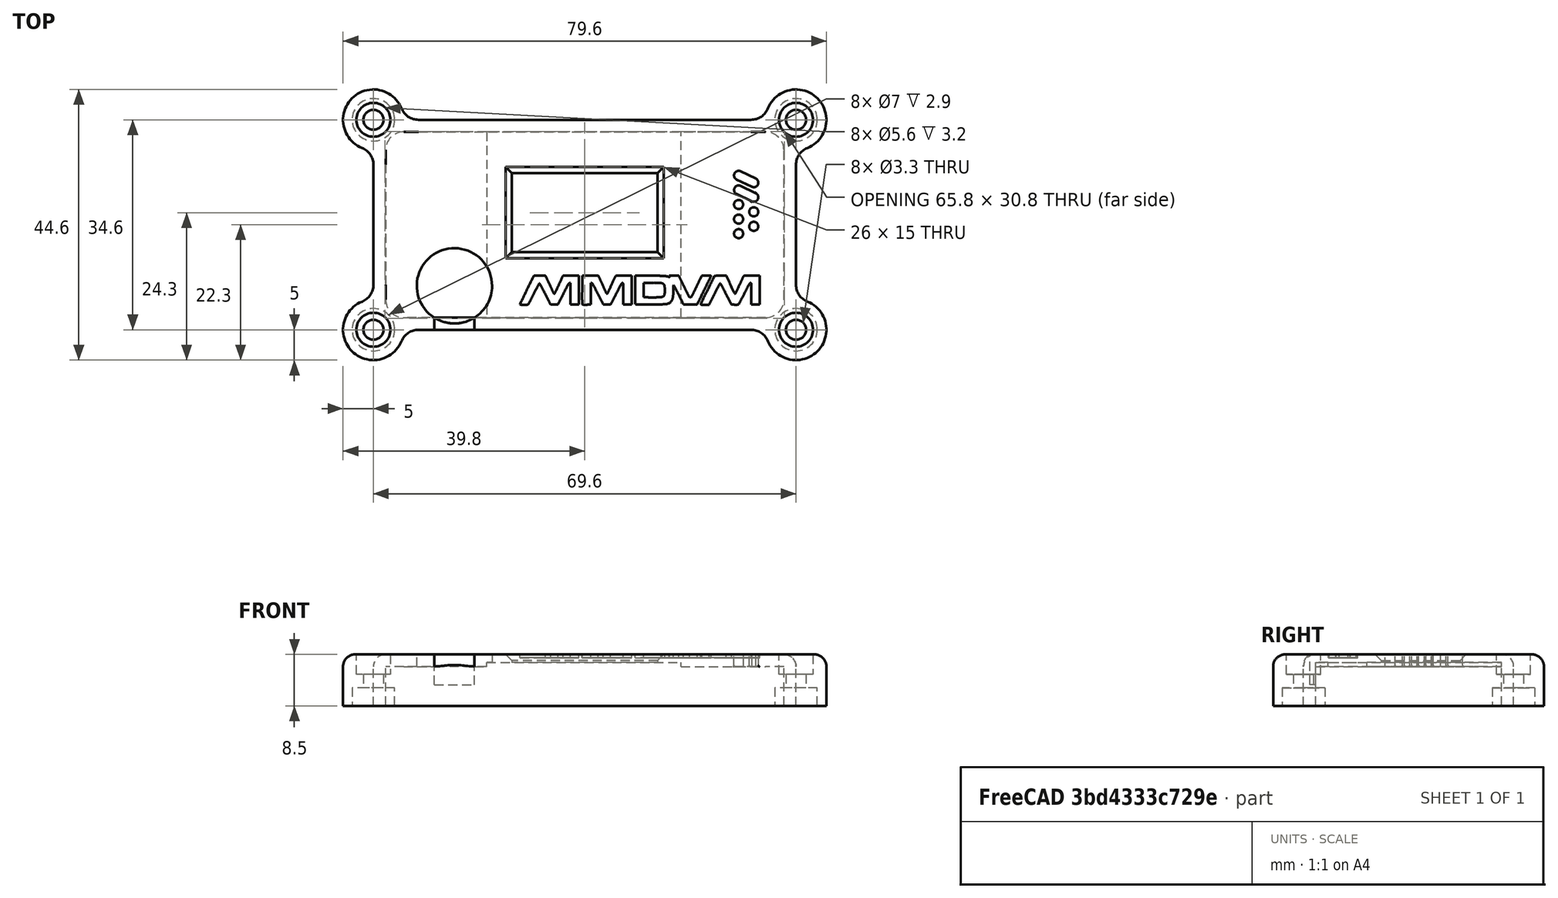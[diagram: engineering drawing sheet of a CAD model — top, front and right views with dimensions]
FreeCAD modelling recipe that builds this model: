
FCSTD DOCUMENT  (FreeCAD 0.18R13964 (Git))
Label: MMDVM_HS_Top-PCB-v1.7-SLIM
License: CreativeCommons Attribution-NonCommercial-ShareAlike
LicenseURL: http://creativecommons.org/licenses/by-nc-sa/4.0/
objects: Sketcher::SketchObject×11, PartDesign::Pocket×6, Part::Feature×5, PartDesign::Fillet×4, Part::Cut×2, Part::FeaturePython×2, PartDesign::Pad×1, PartDesign::Chamfer×1, PartDesign::Hole×1, Part::MultiFuse×1, PartDesign::Body×1, Part::Extrusion×1, Mesh::Feature×1
note: 44 computed .brp shape members not serialized (recipe doc carries the construction recipe); baked Part::Feature solids carry a one-line shape summary decoded from their .brp

FEATURE [Sketcher::SketchObject] Sketch
  MapMode = 5
  Support = -> [XY_Plane]
  sketch-geometry (24):
    g0: LineSegment [constr] StartX=-32.5 StartY=15 StartZ=0 EndX=32.5 EndY=15 EndZ=0
    g1: LineSegment [constr] StartX=32.5 StartY=15 StartZ=0 EndX=32.5 EndY=-15 EndZ=0
    g2: LineSegment [constr] StartX=32.5 StartY=-15 StartZ=0 EndX=-32.5 EndY=-15 EndZ=0
    g3: LineSegment [constr] StartX=-32.5 StartY=-15 StartZ=0 EndX=-32.5 EndY=15 EndZ=0
    g4: LineSegment [constr] StartX=-29 StartY=11.5 StartZ=0 EndX=29 EndY=11.5 EndZ=0
    g5: LineSegment [constr] StartX=29 StartY=11.5 StartZ=0 EndX=29 EndY=-11.5 EndZ=0
    g6: LineSegment [constr] StartX=29 StartY=-11.5 StartZ=0 EndX=-29 EndY=-11.5 EndZ=0
    g7: LineSegment [constr] StartX=-29 StartY=-11.5 StartZ=0 EndX=-29 EndY=11.5 EndZ=0
    g8: Circle CenterX=-29 CenterY=11.5 CenterZ=0 NormalX=0 NormalY=0 NormalZ=1 AngleXU=0 Radius=1.375
    g9: Circle CenterX=29 CenterY=11.5 CenterZ=0 NormalX=0 NormalY=0 NormalZ=1 AngleXU=0 Radius=1.375
    g10: Circle CenterX=29 CenterY=-11.5 CenterZ=0 NormalX=0 NormalY=0 NormalZ=1 AngleXU=0 Radius=1.375
    g11: Circle CenterX=-29 CenterY=-11.5 CenterZ=0 NormalX=0 NormalY=0 NormalZ=1 AngleXU=0 Radius=1.375
    g12: LineSegment [constr] StartX=-29.5 StartY=12 StartZ=0 EndX=29.5 EndY=12 EndZ=0
    g13: LineSegment [constr] StartX=29.5 StartY=12 StartZ=0 EndX=29.5 EndY=-12 EndZ=0
    g14: LineSegment [constr] StartX=29.5 StartY=-12 StartZ=0 EndX=-29.5 EndY=-12 EndZ=0
    g15: LineSegment [constr] StartX=-29.5 StartY=-12 StartZ=0 EndX=-29.5 EndY=12 EndZ=0
    g16: ArcOfCircle CenterX=-29.5 CenterY=12 CenterZ=0 NormalX=0 NormalY=0 NormalZ=1 AngleXU=0 Radius=3 StartAngle=1.5708 EndAngle=3.1416
    g17: ArcOfCircle CenterX=29.5 CenterY=12 CenterZ=0 NormalX=0 NormalY=0 NormalZ=1 AngleXU=0 Radius=3 StartAngle=1.42077e-07 EndAngle=1.5708
    g18: ArcOfCircle CenterX=29.5 CenterY=-12 CenterZ=0 NormalX=0 NormalY=0 NormalZ=1 AngleXU=0 Radius=3 StartAngle=4.71239 EndAngle=6.28319
    g19: ArcOfCircle CenterX=-29.5 CenterY=-12 CenterZ=0 NormalX=0 NormalY=0 NormalZ=1 AngleXU=0 Radius=3 StartAngle=3.14159 EndAngle=4.71239
    g20: LineSegment StartX=-29.5 StartY=15 StartZ=0 EndX=29.5 EndY=15 EndZ=0
    g21: LineSegment StartX=32.5 StartY=12 StartZ=0 EndX=32.5 EndY=-12 EndZ=0
    g22: LineSegment StartX=29.5 StartY=-15 StartZ=0 EndX=-29.5 EndY=-15 EndZ=0
    g23: LineSegment StartX=-32.5 StartY=-12 StartZ=0 EndX=-32.5 EndY=12 EndZ=0
  constraints (68):
    c: Coincident(g0,g1)
    c: Coincident(g1,g2)
    c: Coincident(g2,g3)
    c: Coincident(g3,g0)
    c: Horizontal(g0)
    c: Horizontal(g2)
    c: Vertical(g1)
    c: Vertical(g3)
    c: DistanceX(g0,g0) = 65
    c: DistanceY(g1,g1) = 30
    c: Symmetric(g0,g0,g-2)
    c: Symmetric(g0,g1,g-1)
    c: Coincident(g4,g5)
    c: Coincident(g5,g6)
    c: Coincident(g6,g7)
    c: Coincident(g7,g4)
    c: Horizontal(g4)
    c: Horizontal(g6)
    c: Vertical(g5)
    c: Vertical(g7)
    c: DistanceX(g4,g4) = 58
    c: DistanceY(g5,g5) = 23
    c: Symmetric(g4,g5,g-1)
    c: Symmetric(g4,g4,g-2)
    c: Coincident(g8,g4)
    c: Coincident(g9,g4)
    c: Coincident(g10,g5)
    c: Coincident(g11,g6)
    c: Radius(g11) = 1.375
    c: Radius(g8) = 1.375
    c: Radius(g9) = 1.375
    c: Radius(g10) = 1.375
    c: Coincident(g12,g13)
    c: Coincident(g13,g14)
    c: Coincident(g14,g15)
    c: Coincident(g15,g12)
    c: Horizontal(g12)
    c: Horizontal(g14)
    c: Vertical(g13)
    c: Vertical(g15)
    c: DistanceX(g4,g12) = 0.5
    c: DistanceY(g4,g12) = 0.5
    c: DistanceY(g13,g5) = 0.5
    c: DistanceX(g14,g6) = 0.5
    c: Coincident(g16,g12)
    c: Radius(g16) = 3
    c: Coincident(g17,g12)
    c: Radius(g17) = 3
    c: Coincident(g18,g13)
    c: Radius(g18) = 3
    c: Coincident(g19,g14)
    c: Radius(g19) = 3
    c: PointOnObject(g16,g0)
    c: PointOnObject(g17,g1)
    c: PointOnObject(g18,g2)
    c: PointOnObject(g19,g3)
    c: Coincident(g20,g16)
    c: Horizontal(g20)
    c: Coincident(g20,g17)
    c: Coincident(g21,g17)
    c: Vertical(g21)
    c: Coincident(g18,g21)
    c: Coincident(g22,g18)
    c: Horizontal(g22)
    c: Coincident(g19,g22)
    c: Coincident(g23,g19)
    c: Vertical(g23)
    c: Coincident(g23,g16)
FEATURE [Sketcher::SketchObject] Sketch001
  MapMode = 5
  Support = -> [XY_Plane]
  expr: Constraints[8] = Sketch.Constraints[8]
  expr: Constraints[41] = Sketch.Constraints[41]
  expr: Constraints[9] = Sketch.Constraints[9]
  expr: Constraints[45] = Sketch.Constraints[45]
  expr: Constraints[43] = Sketch.Constraints[43]
  expr: Constraints[42] = Sketch.Constraints[42]
  expr: Constraints[20] = Sketch.Constraints[20]
  expr: Constraints[21] = Sketch.Constraints[21]
  expr: Constraints[28] = Sketch.Constraints[28]
  expr: Constraints[29] = Sketch.Constraints[29]
  expr: Constraints[30] = Sketch.Constraints[30]
  expr: Constraints[40] = Sketch.Constraints[40]
  expr: Constraints[31] = Sketch.Constraints[31]
  expr: Constraints[47] = Sketch.Constraints[47]
  expr: Constraints[49] = Sketch.Constraints[49]
  expr: Constraints[51] = Sketch.Constraints[51]
  sketch-geometry (64):
    g0: LineSegment [constr] StartX=-32.5 StartY=15 StartZ=0 EndX=32.5 EndY=15 EndZ=0
    g1: LineSegment [constr] StartX=32.5 StartY=15 StartZ=0 EndX=32.5 EndY=-15 EndZ=0
    g2: LineSegment [constr] StartX=32.5 StartY=-15 StartZ=0 EndX=-32.5 EndY=-15 EndZ=0
    g3: LineSegment [constr] StartX=-32.5 StartY=-15 StartZ=0 EndX=-32.5 EndY=15 EndZ=0
    g4: LineSegment [constr] StartX=-29 StartY=11.5 StartZ=0 EndX=29 EndY=11.5 EndZ=0
    g5: LineSegment [constr] StartX=29 StartY=11.5 StartZ=0 EndX=29 EndY=-11.5 EndZ=0
    g6: LineSegment [constr] StartX=29 StartY=-11.5 StartZ=0 EndX=-29 EndY=-11.5 EndZ=0
    g7: LineSegment [constr] StartX=-29 StartY=-11.5 StartZ=0 EndX=-29 EndY=11.5 EndZ=0
    g8: Circle [constr] CenterX=-29 CenterY=11.5 CenterZ=0 NormalX=0 NormalY=0 NormalZ=1 AngleXU=0 Radius=1.375
    g9: Circle [constr] CenterX=29 CenterY=11.5 CenterZ=0 NormalX=0 NormalY=0 NormalZ=1 AngleXU=0 Radius=1.375
    g10: Circle [constr] CenterX=29 CenterY=-11.5 CenterZ=0 NormalX=0 NormalY=0 NormalZ=1 AngleXU=0 Radius=1.375
    g11: Circle [constr] CenterX=-29 CenterY=-11.5 CenterZ=0 NormalX=0 NormalY=0 NormalZ=1 AngleXU=0 Radius=1.375
    g12: LineSegment [constr] StartX=-29.5 StartY=12 StartZ=0 EndX=29.5 EndY=12 EndZ=0
    g13: LineSegment [constr] StartX=29.5 StartY=12 StartZ=0 EndX=29.5 EndY=-12 EndZ=0
    g14: LineSegment [constr] StartX=29.5 StartY=-12 StartZ=0 EndX=-29.5 EndY=-12 EndZ=0
    g15: LineSegment [constr] StartX=-29.5 StartY=-12 StartZ=0 EndX=-29.5 EndY=12 EndZ=0
    g16: ArcOfCircle [constr] CenterX=-29.5 CenterY=12 CenterZ=0 NormalX=0 NormalY=0 NormalZ=1 AngleXU=0 Radius=3 StartAngle=1.5708 EndAngle=3.14159
    g17: ArcOfCircle [constr] CenterX=29.5 CenterY=12 CenterZ=0 NormalX=0 NormalY=0 NormalZ=1 AngleXU=0 Radius=3 StartAngle=2.8425e-08 EndAngle=1.5708
    g18: ArcOfCircle [constr] CenterX=29.5 CenterY=-12 CenterZ=0 NormalX=0 NormalY=0 NormalZ=1 AngleXU=0 Radius=3 StartAngle=4.71239 EndAngle=6.28319
    g19: ArcOfCircle [constr] CenterX=-29.5 CenterY=-12 CenterZ=0 NormalX=0 NormalY=0 NormalZ=1 AngleXU=0 Radius=3 StartAngle=3.14159 EndAngle=4.71239
    g20: LineSegment [constr] StartX=-29.5 StartY=15 StartZ=0 EndX=29.5 EndY=15 EndZ=0
    g21: LineSegment [constr] StartX=32.5 StartY=12 StartZ=0 EndX=32.5 EndY=-12 EndZ=0
    g22: LineSegment [constr] StartX=29.5 StartY=-15 StartZ=0 EndX=-29.5 EndY=-15 EndZ=0
    g23: LineSegment [constr] StartX=-32.5 StartY=-12 StartZ=0 EndX=-32.5 EndY=12 EndZ=0
    g24: ArcOfCircle [constr] CenterX=-29.5 CenterY=12 CenterZ=0 NormalX=0 NormalY=0 NormalZ=1 AngleXU=0 Radius=3.3 StartAngle=1.5708 EndAngle=3.14159
    g25: ArcOfCircle [constr] CenterX=29.5 CenterY=12 CenterZ=0 NormalX=0 NormalY=0 NormalZ=1 AngleXU=0 Radius=3.3 StartAngle=-2.2e-10 EndAngle=1.5708
    g26: ArcOfCircle [constr] CenterX=29.5 CenterY=-12 CenterZ=0 NormalX=0 NormalY=0 NormalZ=1 AngleXU=0 Radius=3.3 StartAngle=4.71239 EndAngle=6.28319
    g27: ArcOfCircle [constr] CenterX=-29.5 CenterY=-12 CenterZ=0 NormalX=0 NormalY=0 NormalZ=1 AngleXU=0 Radius=3.3 StartAngle=3.14159 EndAngle=4.71239
    g28: LineSegment [constr] StartX=-32.8 StartY=12 StartZ=0 EndX=-32.8 EndY=-12 EndZ=0
    g29: LineSegment [constr] StartX=-29.5 StartY=15.3 StartZ=0 EndX=29.5 EndY=15.3 EndZ=0
    g30: LineSegment [constr] StartX=32.8 StartY=12 StartZ=0 EndX=32.8 EndY=-12 EndZ=0
    g31: LineSegment [constr] StartX=29.5 StartY=-15.3 StartZ=0 EndX=-29.5 EndY=-15.3 EndZ=0
    g32: LineSegment [constr] StartX=-34.8 StartY=17.3 StartZ=0 EndX=34.8 EndY=17.3 EndZ=0
    g33: LineSegment [constr] StartX=34.8 StartY=17.3 StartZ=0 EndX=34.8 EndY=-17.3 EndZ=0
    g34: LineSegment [constr] StartX=34.8 StartY=-17.3 StartZ=0 EndX=-34.8 EndY=-17.3 EndZ=0
    g35: LineSegment [constr] StartX=-34.8 StartY=-17.3 StartZ=0 EndX=-34.8 EndY=17.3 EndZ=0
    g36: Circle [constr] CenterX=34.8 CenterY=17.3 CenterZ=0 NormalX=0 NormalY=0 NormalZ=1 AngleXU=0 Radius=5
    g37: Circle [constr] CenterX=34.8 CenterY=-17.3 CenterZ=0 NormalX=0 NormalY=0 NormalZ=1 AngleXU=0 Radius=5
    g38: Circle [constr] CenterX=-34.8 CenterY=-17.3 CenterZ=0 NormalX=0 NormalY=0 NormalZ=1 AngleXU=0 Radius=5
    g39: Circle [constr] CenterX=-34.8 CenterY=17.3 CenterZ=0 NormalX=0 NormalY=0 NormalZ=1 AngleXU=0 Radius=5
    g40: Circle [constr] CenterX=27.3838 CenterY=20.3 CenterZ=0 NormalX=0 NormalY=0 NormalZ=1 AngleXU=0 Radius=3
    g41: Circle [constr] CenterX=-27.3838 CenterY=20.3 CenterZ=0 NormalX=0 NormalY=0 NormalZ=1 AngleXU=0 Radius=3
    g42: Circle [constr] CenterX=-37.8 CenterY=9.8838 CenterZ=0 NormalX=0 NormalY=0 NormalZ=1 AngleXU=0 Radius=3
    g43: Circle [constr] CenterX=-37.8 CenterY=-9.8838 CenterZ=0 NormalX=0 NormalY=0 NormalZ=1 AngleXU=0 Radius=3
    g44: Circle [constr] CenterX=-27.3838 CenterY=-20.3 CenterZ=0 NormalX=0 NormalY=0 NormalZ=1 AngleXU=0 Radius=3
    g45: Circle [constr] CenterX=27.3838 CenterY=-20.3 CenterZ=0 NormalX=0 NormalY=0 NormalZ=1 AngleXU=0 Radius=3
    g46: Circle [constr] CenterX=37.8 CenterY=-9.8838 CenterZ=0 NormalX=0 NormalY=0 NormalZ=1 AngleXU=0 Radius=3
    g47: Circle [constr] CenterX=37.8 CenterY=9.8838 CenterZ=0 NormalX=0 NormalY=0 NormalZ=1 AngleXU=0 Radius=3
    g48: ArcOfCircle CenterX=34.8 CenterY=17.3 CenterZ=0 NormalX=0 NormalY=0 NormalZ=1 AngleXU=0 Radius=5 StartAngle=5.09679 EndAngle=9.04038
    g49: ArcOfCircle CenterX=27.3838 CenterY=20.3 CenterZ=0 NormalX=0 NormalY=0 NormalZ=1 AngleXU=0 Radius=3 StartAngle=4.71239 EndAngle=5.89879
    g50: ArcOfCircle CenterX=37.8 CenterY=9.8838 CenterZ=0 NormalX=0 NormalY=0 NormalZ=1 AngleXU=0 Radius=3 StartAngle=1.95519 EndAngle=3.14159
    g51: ArcOfCircle CenterX=37.8 CenterY=-9.8838 CenterZ=0 NormalX=0 NormalY=0 NormalZ=1 AngleXU=0 Radius=3 StartAngle=3.14159 EndAngle=4.32799
    g52: ArcOfCircle CenterX=34.8 CenterY=-17.3 CenterZ=0 NormalX=0 NormalY=0 NormalZ=1 AngleXU=0 Radius=5 StartAngle=3.52599 EndAngle=7.46958
    g53: ArcOfCircle CenterX=27.3838 CenterY=-20.3 CenterZ=0 NormalX=0 NormalY=0 NormalZ=1 AngleXU=0 Radius=3 StartAngle=0.384397 EndAngle=1.5708
    g54: ArcOfCircle CenterX=-27.3838 CenterY=-20.3 CenterZ=0 NormalX=0 NormalY=0 NormalZ=1 AngleXU=0 Radius=3 StartAngle=1.5708 EndAngle=2.7572
    g55: ArcOfCircle CenterX=-34.8 CenterY=-17.3 CenterZ=0 NormalX=0 NormalY=0 NormalZ=1 AngleXU=0 Radius=5 StartAngle=1.95519 EndAngle=5.89879
    g56: ArcOfCircle CenterX=-37.8 CenterY=-9.8838 CenterZ=0 NormalX=0 NormalY=0 NormalZ=1 AngleXU=0 Radius=3 StartAngle=5.09679 EndAngle=6.28319
    g57: ArcOfCircle CenterX=-37.8 CenterY=9.8838 CenterZ=0 NormalX=0 NormalY=0 NormalZ=1 AngleXU=0 Radius=3 StartAngle=6.28319 EndAngle=7.46958
    g58: ArcOfCircle CenterX=-34.8 CenterY=17.3 CenterZ=0 NormalX=0 NormalY=0 NormalZ=1 AngleXU=0 Radius=5 StartAngle=0.384397 EndAngle=4.32799
    g59: ArcOfCircle CenterX=-27.3838 CenterY=20.3 CenterZ=0 NormalX=0 NormalY=0 NormalZ=1 AngleXU=0 Radius=3 StartAngle=3.52599 EndAngle=4.71239
    g60: LineSegment StartX=-27.3838 StartY=17.3 StartZ=0 EndX=27.3838 EndY=17.3 EndZ=0
    g61: LineSegment StartX=34.8 StartY=9.8838 StartZ=0 EndX=34.8 EndY=-9.8838 EndZ=0
    g62: LineSegment StartX=27.3838 StartY=-17.3 StartZ=0 EndX=-27.3838 EndY=-17.3 EndZ=0
    g63: LineSegment StartX=-34.8 StartY=-9.8838 StartZ=0 EndX=-34.8 EndY=9.8838 EndZ=0
  constraints (184):
    c: Coincident(g0,g1)
    c: Coincident(g1,g2)
    c: Coincident(g2,g3)
    c: Coincident(g3,g0)
    c: Horizontal(g0)
    c: Horizontal(g2)
    c: Vertical(g1)
    c: Vertical(g3)
    c: DistanceX(g0,g0) = 65
    c: DistanceY(g1,g1) = 30
    c: Symmetric(g0,g0,g-2)
    c: Symmetric(g0,g1,g-1)
    c: Coincident(g4,g5)
    c: Coincident(g5,g6)
    c: Coincident(g6,g7)
    c: Coincident(g7,g4)
    c: Horizontal(g4)
    c: Horizontal(g6)
    c: Vertical(g5)
    c: Vertical(g7)
    c: DistanceX(g4,g4) = 58
    c: DistanceY(g5,g5) = 23
    c: Symmetric(g4,g5,g-1)
    c: Symmetric(g4,g4,g-2)
    c: Coincident(g8,g4)
    c: Coincident(g9,g4)
    c: Coincident(g10,g5)
    c: Coincident(g11,g6)
    c: Radius(g11) = 1.375
    c: Radius(g8) = 1.375
    c: Radius(g9) = 1.375
    c: Radius(g10) = 1.375
    c: Coincident(g12,g13)
    c: Coincident(g13,g14)
    c: Coincident(g14,g15)
    c: Coincident(g15,g12)
    c: Horizontal(g12)
    c: Horizontal(g14)
    c: Vertical(g13)
    c: Vertical(g15)
    c: DistanceX(g4,g12) = 0.5
    c: DistanceY(g4,g12) = 0.5
    c: DistanceY(g13,g5) = 0.5
    c: DistanceX(g14,g6) = 0.5
    c: Coincident(g16,g12)
    c: Radius(g16) = 3
    c: Coincident(g17,g12)
    c: Radius(g17) = 3
    c: Coincident(g18,g13)
    c: Radius(g18) = 3
    c: Coincident(g19,g14)
    c: Radius(g19) = 3
    c: PointOnObject(g16,g0)
    c: PointOnObject(g17,g1)
    c: PointOnObject(g18,g2)
    c: PointOnObject(g19,g3)
    c: Coincident(g20,g16)
    c: Horizontal(g20)
    c: Coincident(g20,g17)
    c: Coincident(g21,g17)
    c: Vertical(g21)
    c: Coincident(g18,g21)
    c: Coincident(g22,g18)
    c: Horizontal(g22)
    c: Coincident(g19,g22)
    c: Coincident(g23,g19)
    c: Vertical(g23)
    c: Coincident(g23,g16)
    c: Coincident(g24,g12)
    c: Radius(g24) = 3.3
    c: Coincident(g25,g12)
    c: Radius(g25) = 3.3
    c: Coincident(g26,g13)
    c: Radius(g26) = 3.3
    c: Coincident(g27,g14)
    c: Radius(g27) = 3.3
    c: Vertical(g28)
    c: DistanceX(g28,g2) = 0.3
    c: Coincident(g27,g28)
    c: Coincident(g28,g24)
    c: Horizontal(g29)
    c: DistanceY(g0,g29) = 0.3
    c: Coincident(g24,g29)
    c: Coincident(g25,g29)
    c: Vertical(g30)
    c: DistanceX(g0,g30) = 0.3
    c: Coincident(g25,g30)
    c: Coincident(g30,g26)
    c: Horizontal(g31)
    c: DistanceY(g31,g1) = 0.3
    c: Coincident(g31,g26)
    c: Coincident(g31,g27)
    c: Coincident(g32,g33)
    c: Coincident(g33,g34)
    c: Coincident(g34,g35)
    c: Coincident(g35,g32)
    c: Horizontal(g32)
    c: Horizontal(g34)
    c: Vertical(g33)
    c: Vertical(g35)
    c: DistanceY(g25,g32) = 2
    c: DistanceX(g25,g32) = 2
    c: DistanceY(g33,g26) = 2
    c: DistanceX(g34,g27) = 2
    c: Coincident(g36,g32)
    c: Coincident(g37,g33)
    c: Coincident(g38,g34)
    c: Coincident(g39,g32)
    c: Radius(g39) = 5
    c: Radius(g38) = 5
    c: Radius(g37) = 5
    c: Radius(g36) = 5
    c: Radius(g40) = 3
    c: Tangent(g40,g36)
    c: Tangent(g40,g32)
    c: Tangent(g47,g36)
    c: Radius(g47) = 3
    c: Tangent(g47,g33)
    c: Radius(g46) = 3
    c: Tangent(g46,g37)
    c: Tangent(g46,g33)
    c: Radius(g45) = 3
    c: Tangent(g45,g37)
    c: Tangent(g45,g34)
    c: Radius(g44) = 3
    c: Tangent(g44,g34)
    c: Tangent(g44,g38)
    c: Radius(g43) = 3
    c: Tangent(g43,g38)
    c: Tangent(g43,g35)
    c: Radius(g42) = 3
    c: Tangent(g42,g35)
    c: Tangent(g42,g39)
    c: Radius(g41) = 3
    c: Tangent(g41,g32)
    c: Tangent(g41,g39)
    c: Coincident(g48,g32)
    c: PointOnObject(g48,g36)
    c: Coincident(g49,g40)
    c: PointOnObject(g49,g40)
    c: Coincident(g50,g47)
    c: PointOnObject(g50,g47)
    c: Coincident(g51,g46)
    c: PointOnObject(g51,g46)
    c: Coincident(g52,g33)
    c: PointOnObject(g52,g37)
    c: Coincident(g53,g45)
    c: PointOnObject(g53,g45)
    c: Coincident(g54,g44)
    c: PointOnObject(g54,g44)
    c: Coincident(g55,g34)
    c: PointOnObject(g55,g38)
    c: Coincident(g56,g43)
    c: PointOnObject(g56,g43)
    c: Coincident(g57,g42)
    c: PointOnObject(g57,g42)
    c: Coincident(g58,g32)
    c: PointOnObject(g58,g39)
    c: Coincident(g59,g41)
    c: PointOnObject(g59,g41)
    c: Coincident(g49,g48)
    c: Coincident(g48,g50)
    c: Coincident(g51,g52)
    c: Coincident(g52,g53)
    c: Coincident(g54,g55)
    c: Coincident(g55,g56)
    c: Coincident(g57,g58)
    c: Coincident(g58,g59)
    c: PointOnObject(g60,g32)
    c: Horizontal(g60)
    c: PointOnObject(g61,g33)
    c: Vertical(g61)
    c: PointOnObject(g62,g34)
    c: Horizontal(g62)
    c: PointOnObject(g63,g35)
    c: Vertical(g63)
    c: Coincident(g59,g60)
    c: Coincident(g60,g49)
    c: Coincident(g50,g61)
    c: Coincident(g61,g51)
    c: Coincident(g53,g62)
    c: Coincident(g54,g62)
    c: Coincident(g56,g63)
    c: Coincident(g57,g63)
FEATURE [PartDesign::Pad] Pad
  Length = 8.5
  Length2 = 100
  Profile = -> Sketch001
  Type = 0
FEATURE [Sketcher::SketchObject] Sketch002
  ExternalGeometry = -> [Pad]
  MapMode = 5
  Placement = pos=(0,0,0) rot=(1,0,0;3.14159rad)
  Support = -> [Pad]
  sketch-geometry (4):
    g0: Circle CenterX=34.8 CenterY=17.3 CenterZ=0 NormalX=0 NormalY=0 NormalZ=1 AngleXU=0 Radius=3.5
    g1: Circle CenterX=34.8 CenterY=-17.3 CenterZ=0 NormalX=0 NormalY=0 NormalZ=1 AngleXU=0 Radius=3.5
    g2: Circle CenterX=-34.8 CenterY=-17.3 CenterZ=0 NormalX=0 NormalY=0 NormalZ=1 AngleXU=0 Radius=3.5
    g3: Circle CenterX=-34.8 CenterY=17.3 CenterZ=0 NormalX=0 NormalY=0 NormalZ=1 AngleXU=0 Radius=3.5
  constraints (8):
    c: Coincident(g0,g-3)
    c: Radius(g0) = 3.5
    c: Coincident(g1,g-6)
    c: Radius(g1) = 3.5
    c: Coincident(g2,g-5)
    c: Radius(g2) = 3.5
    c: Coincident(g3,g-4)
    c: Radius(g3) = 3.5
FEATURE [PartDesign::Pocket] Pocket
  BaseFeature = -> Pad
  Length = 3
  Length2 = 1
  Profile = -> Sketch002
  Type = 0
FEATURE [Sketcher::SketchObject] Sketch003
  MapMode = 5
  Placement = pos=(0,0,0) rot=(1,0,0;3.14159rad)
  Support = -> [Pocket]
  expr: Constraints[8] = Sketch.Constraints[8]
  expr: Constraints[39] = Sketch.Constraints[40]
  expr: Constraints[30] = Sketch.Constraints[31]
  expr: Constraints[27] = Sketch.Constraints[28]
  expr: Constraints[29] = Sketch.Constraints[30]
  expr: Constraints[28] = Sketch.Constraints[29]
  expr: Constraints[20] = -Sketch.Constraints[21]
  expr: Constraints[19] = Sketch.Constraints[20]
  expr: Constraints[42] = Sketch.Constraints[43]
  expr: Constraints[41] = -Sketch.Constraints[42]
  expr: Constraints[9] = -Sketch.Constraints[9]
  expr: Constraints[40] = -Sketch.Constraints[41]
  sketch-geometry (32):
    g0: LineSegment [constr] StartX=-32.5 StartY=-15 StartZ=0 EndX=32.5 EndY=-15 EndZ=0
    g1: LineSegment [constr] StartX=32.5 StartY=-15 StartZ=0 EndX=32.5 EndY=15 EndZ=0
    g2: LineSegment [constr] StartX=32.5 StartY=15 StartZ=0 EndX=-32.5 EndY=15 EndZ=0
    g3: LineSegment [constr] StartX=-32.5 StartY=15 StartZ=0 EndX=-32.5 EndY=-15 EndZ=0
    g4: LineSegment [constr] StartX=-29 StartY=-11.5 StartZ=0 EndX=29 EndY=-11.5 EndZ=0
    g5: LineSegment [constr] StartX=29 StartY=-11.5 StartZ=0 EndX=29 EndY=11.5 EndZ=0
    g6: LineSegment [constr] StartX=29 StartY=11.5 StartZ=0 EndX=-29 EndY=11.5 EndZ=0
    g7: LineSegment [constr] StartX=-29 StartY=11.5 StartZ=0 EndX=-29 EndY=-11.5 EndZ=0
    g8: Circle [constr] CenterX=-29 CenterY=-11.5 CenterZ=0 NormalX=0 NormalY=0 NormalZ=1 AngleXU=0 Radius=1.375
    g9: Circle [constr] CenterX=29 CenterY=-11.5 CenterZ=0 NormalX=0 NormalY=0 NormalZ=1 AngleXU=0 Radius=1.375
    g10: Circle [constr] CenterX=29 CenterY=11.5 CenterZ=0 NormalX=0 NormalY=0 NormalZ=1 AngleXU=0 Radius=1.375
    g11: Circle [constr] CenterX=-29 CenterY=11.5 CenterZ=0 NormalX=0 NormalY=0 NormalZ=1 AngleXU=0 Radius=1.375
    g12: LineSegment [constr] StartX=-29.5 StartY=-12 StartZ=0 EndX=29.5 EndY=-12 EndZ=0
    g13: LineSegment [constr] StartX=29.5 StartY=-12 StartZ=0 EndX=29.5 EndY=12 EndZ=0
    g14: LineSegment [constr] StartX=29.5 StartY=12 StartZ=0 EndX=-29.5 EndY=12 EndZ=0
    g15: LineSegment [constr] StartX=-29.5 StartY=12 StartZ=0 EndX=-29.5 EndY=-12 EndZ=0
    g16: LineSegment [constr] StartX=-29.5121 StartY=-15 StartZ=0 EndX=29.5 EndY=-15 EndZ=0
    g17: LineSegment [constr] StartX=32.5 StartY=-12 StartZ=0 EndX=32.5 EndY=12 EndZ=0
    g18: LineSegment [constr] StartX=29.5 StartY=15 StartZ=0 EndX=-29.5121 EndY=15 EndZ=0
    g19: LineSegment [constr] StartX=-32.5 StartY=12 StartZ=0 EndX=-32.5 EndY=-12 EndZ=0
    g20: ArcOfCircle [constr] CenterX=-29.5 CenterY=12 CenterZ=0 NormalX=0 NormalY=0 NormalZ=1 AngleXU=0 Radius=3.00002 StartAngle=1.57483 EndAngle=3.1416
    g21: ArcOfCircle [constr] CenterX=29.5 CenterY=12 CenterZ=0 NormalX=0 NormalY=0 NormalZ=1 AngleXU=0 Radius=3 StartAngle=6.28318 EndAngle=7.85399
    g22: ArcOfCircle [constr] CenterX=29.5 CenterY=-12 CenterZ=0 NormalX=0 NormalY=0 NormalZ=1 AngleXU=0 Radius=3 StartAngle=4.71238 EndAngle=6.28319
    g23: ArcOfCircle [constr] CenterX=-29.5 CenterY=-12 CenterZ=0 NormalX=0 NormalY=0 NormalZ=1 AngleXU=0 Radius=3.00002 StartAngle=3.14159 EndAngle=4.70836
    g24: LineSegment StartX=-29.8 StartY=15.3 StartZ=0 EndX=29.8 EndY=15.3 EndZ=0
    g25: LineSegment StartX=32.8 StartY=12.3 StartZ=0 EndX=32.8 EndY=-12.3 EndZ=0
    g26: LineSegment StartX=29.8 StartY=-15.3 StartZ=0 EndX=-29.8 EndY=-15.3 EndZ=0
    g27: LineSegment StartX=-32.8 StartY=-12.3 StartZ=0 EndX=-32.8 EndY=12.3 EndZ=0
    g28: ArcOfCircle CenterX=29.8 CenterY=12.3 CenterZ=0 NormalX=0 NormalY=0 NormalZ=1 AngleXU=0 Radius=3 StartAngle=0 EndAngle=1.5708
    g29: ArcOfCircle CenterX=29.8 CenterY=-12.3 CenterZ=0 NormalX=0 NormalY=0 NormalZ=1 AngleXU=0 Radius=3 StartAngle=4.71239 EndAngle=6.28319
    g30: ArcOfCircle CenterX=-29.8 CenterY=-12.3 CenterZ=0 NormalX=0 NormalY=0 NormalZ=1 AngleXU=0 Radius=3 StartAngle=3.14159 EndAngle=4.71239
    g31: ArcOfCircle CenterX=-29.8 CenterY=12.3 CenterZ=0 NormalX=0 NormalY=0 NormalZ=1 AngleXU=0 Radius=3 StartAngle=1.5708 EndAngle=3.14159
  constraints (83):
    c: Coincident(g0,g1)
    c: Coincident(g1,g2)
    c: Coincident(g2,g3)
    c: Coincident(g3,g0)
    c: Horizontal(g0)
    c: Horizontal(g2)
    c: Vertical(g1)
    c: Vertical(g3)
    c: DistanceX(g0,g0) = 65
    c: DistanceY(g1,g1) = -30
    c: Symmetric(g0,g0,g-2)
    c: Symmetric(g0,g1,g-1)
    c: Coincident(g4,g5)
    c: Coincident(g5,g6)
    c: Coincident(g6,g7)
    c: Horizontal(g4)
    c: Horizontal(g6)
    c: Vertical(g5)
    c: Vertical(g7)
    c: DistanceX(g4,g4) = 58
    c: DistanceY(g5,g5) = -23
    c: Symmetric(g4,g5,g-1)
    c: Symmetric(g4,g4,g-2)
    c: Coincident(g8,g4)
    c: Coincident(g9,g4)
    c: Coincident(g10,g5)
    c: Coincident(g11,g6)
    c: Radius(g11) = 1.375
    c: Radius(g8) = 1.375
    c: Radius(g9) = 1.375
    c: Radius(g10) = 1.375
    c: Coincident(g12,g13)
    c: Coincident(g13,g14)
    c: Coincident(g14,g15)
    c: Coincident(g15,g12)
    c: Horizontal(g12)
    c: Horizontal(g14)
    c: Vertical(g13)
    c: Vertical(g15)
    c: DistanceX(g4,g12) = 0.5
    c: DistanceY(g4,g12) = -0.5
    c: DistanceY(g13,g5) = -0.5
    c: DistanceX(g14,g6) = 0.5
    c: PointOnObject(g16,g0)
    c: PointOnObject(g17,g1)
    c: PointOnObject(g18,g2)
    c: PointOnObject(g19,g3)
    c: Horizontal(g16)
    c: Vertical(g17)
    c: Horizontal(g18)
    c: Vertical(g19)
    c: Coincident(g20,g14)
    c: Coincident(g20,g18)
    c: Coincident(g20,g19)
    c: Coincident(g21,g13)
    c: Coincident(g21,g17)
    c: Coincident(g21,g18)
    c: Coincident(g22,g12)
    c: Coincident(g22,g16)
    c: Coincident(g22,g17)
    c: Coincident(g23,g12)
    c: Coincident(g23,g19)
    c: Coincident(g23,g16)
    c: Horizontal(g24)
    c: Horizontal(g26)
    c: Vertical(g25)
    c: Vertical(g27)
    c: Tangent(g24,g28) = 1.5708
    c: Tangent(g25,g28) = 1.5708
    c: Tangent(g25,g29) = 1.5708
    c: Tangent(g26,g29) = 1.5708
    c: Tangent(g26,g30) = 1.5708
    c: Tangent(g27,g30) = 1.5708
    c: Tangent(g27,g31) = 1.5708
    c: Tangent(g24,g31) = 1.5708
    c: Radius(g31) = 3
    c: Radius(g28) = 3
    c: Radius(g29) = 3
    c: Radius(g30) = 3
    c: DistanceY(g1,g24) = 0.3
    c: DistanceX(g17,g25) = 0.3
    c: DistanceY(g26,g16) = 0.3
    c: DistanceX(g27,g19) = 0.3
FEATURE [PartDesign::Pocket] Pocket001
  BaseFeature = -> Pocket
  Length = 6.5
  Length2 = 100
  Profile = -> Sketch003
  Type = 0
FEATURE [Sketcher::SketchObject] Sketch004
  ExternalGeometry = -> [Pocket001]
  MapMode = 5
  Placement = pos=(0,0,8.5) rot=(0,0,1;0rad)
  Support = -> [Pocket001]
  sketch-geometry (32):
    g0: LineSegment StartX=-27.3838 StartY=17.3 StartZ=0 EndX=-31.8 EndY=17.3 EndZ=0
    g1: LineSegment StartX=-34.8 StartY=9.8838 StartZ=0 EndX=-34.8 EndY=14.3 EndZ=0
    g2: Circle [constr] CenterX=-31.8 CenterY=14.3 CenterZ=0 NormalX=0 NormalY=0 NormalZ=1 AngleXU=0 Radius=3
    g3: ArcOfCircle CenterX=-31.8 CenterY=14.3 CenterZ=0 NormalX=0 NormalY=0 NormalZ=1 AngleXU=0 Radius=3 StartAngle=1.5708 EndAngle=3.14159
    g4: LineSegment StartX=-41.7809 StartY=24.2149 StartZ=0 EndX=-27.3838 EndY=24.2149 EndZ=0
    g5: LineSegment StartX=-41.7809 StartY=9.8838 StartZ=0 EndX=-41.7809 EndY=24.2149 EndZ=0
    g6: LineSegment StartX=-27.3838 StartY=24.2149 StartZ=0 EndX=-27.3838 EndY=17.3 EndZ=0
    g7: LineSegment StartX=-41.7809 StartY=9.8838 StartZ=0 EndX=-34.8 EndY=9.8838 EndZ=0
    g8: LineSegment StartX=27.3838 StartY=17.3 StartZ=0 EndX=31.8 EndY=17.3 EndZ=0
    g9: LineSegment StartX=34.8 StartY=9.8838 StartZ=0 EndX=34.8 EndY=14.3 EndZ=0
    g10: Circle [constr] CenterX=31.8 CenterY=14.3 CenterZ=0 NormalX=0 NormalY=0 NormalZ=1 AngleXU=0 Radius=3
    g11: ArcOfCircle CenterX=31.8 CenterY=14.3 CenterZ=0 NormalX=0 NormalY=0 NormalZ=1 AngleXU=0 Radius=3 StartAngle=4.4834e-08 EndAngle=1.5708
    g12: LineSegment StartX=41.7622 StartY=24.6512 StartZ=0 EndX=27.3838 EndY=24.6512 EndZ=0
    g13: LineSegment StartX=41.7622 StartY=9.8838 StartZ=0 EndX=41.7622 EndY=24.6512 EndZ=0
    g14: LineSegment StartX=27.3838 StartY=24.6512 StartZ=0 EndX=27.3838 EndY=17.3 EndZ=0
    g15: LineSegment StartX=41.7622 StartY=9.8838 StartZ=0 EndX=34.8 EndY=9.8838 EndZ=0
    g16: LineSegment StartX=-34.8 StartY=-9.8838 StartZ=0 EndX=-34.8 EndY=-14.3 EndZ=0
    g17: LineSegment StartX=-27.3838 StartY=-17.3 StartZ=0 EndX=-31.8 EndY=-17.3 EndZ=0
    g18: Circle [constr] CenterX=-31.8 CenterY=-14.3 CenterZ=0 NormalX=0 NormalY=0 NormalZ=1 AngleXU=0 Radius=3
    g19: ArcOfCircle CenterX=-31.8 CenterY=-14.3 CenterZ=0 NormalX=0 NormalY=0 NormalZ=1 AngleXU=0 Radius=3 StartAngle=3.14159 EndAngle=4.71239
    g20: LineSegment StartX=-27.3838 StartY=-24.2044 StartZ=0 EndX=-41.4724 EndY=-24.2044 EndZ=0
    g21: LineSegment StartX=-41.4724 StartY=-24.2044 StartZ=0 EndX=-41.4724 EndY=-9.8838 EndZ=0
    g22: LineSegment StartX=-41.4724 StartY=-9.8838 StartZ=0 EndX=-34.8 EndY=-9.8838 EndZ=0
    g23: LineSegment StartX=-27.3838 StartY=-24.2044 StartZ=0 EndX=-27.3838 EndY=-17.3 EndZ=0
    g24: LineSegment StartX=34.8 StartY=-9.8838 StartZ=0 EndX=34.8 EndY=-14.3 EndZ=0
    g25: LineSegment StartX=27.3838 StartY=-17.3 StartZ=0 EndX=31.8 EndY=-17.3 EndZ=0
    g26: Circle [constr] CenterX=31.8 CenterY=-14.3 CenterZ=0 NormalX=0 NormalY=0 NormalZ=1 AngleXU=0 Radius=3
    g27: ArcOfCircle CenterX=31.8 CenterY=-14.3 CenterZ=0 NormalX=0 NormalY=0 NormalZ=1 AngleXU=0 Radius=3 StartAngle=4.71239 EndAngle=6.28319
    g28: LineSegment StartX=41.5436 StartY=-23.6904 StartZ=0 EndX=27.3838 EndY=-23.6904 EndZ=0
    g29: LineSegment StartX=41.5436 StartY=-9.8838 StartZ=0 EndX=41.5436 EndY=-23.6904 EndZ=0
    g30: LineSegment StartX=41.5436 StartY=-9.8838 StartZ=0 EndX=34.8 EndY=-9.8838 EndZ=0
    g31: LineSegment StartX=27.3838 StartY=-23.6904 StartZ=0 EndX=27.3838 EndY=-17.3 EndZ=0
  constraints (88):
    c: PointOnObject(g0,g-3)
    c: Horizontal(g0)
    c: PointOnObject(g1,g-6)
    c: Vertical(g1)
    c: Radius(g2) = 3
    c: Tangent(g2,g0)
    c: Tangent(g2,g1)
    c: Coincident(g3,g2)
    c: PointOnObject(g3,g2)
    c: Coincident(g3,g1)
    c: Coincident(g3,g0)
    c: Coincident(g5,g4)
    c: Horizontal(g4)
    c: Vertical(g5)
    c: Coincident(g6,g4)
    c: Vertical(g6)
    c: Coincident(g7,g5)
    c: Horizontal(g7)
    c: Coincident(g7,g1)
    c: Coincident(g6,g0)
    c: PointOnObject(g8,g-3)
    c: Horizontal(g8)
    c: PointOnObject(g9,g-4)
    c: Vertical(g9)
    c: Radius(g10) = 3
    c: Tangent(g10,g8)
    c: Tangent(g10,g9)
    c: Coincident(g11,g10)
    c: PointOnObject(g11,g10)
    c: Coincident(g11,g8)
    c: Coincident(g11,g9)
    c: Coincident(g13,g12)
    c: Horizontal(g12)
    c: Vertical(g13)
    c: Coincident(g14,g12)
    c: Vertical(g14)
    c: Coincident(g15,g13)
    c: Horizontal(g15)
    c: Coincident(g15,g9)
    c: Coincident(g14,g8)
    c: PointOnObject(g16,g-6)
    c: Vertical(g16)
    c: PointOnObject(g17,g-5)
    c: Horizontal(g17)
    c: Radius(g18) = 3
    c: Tangent(g18,g16)
    c: Tangent(g18,g17)
    c: Coincident(g19,g18)
    c: PointOnObject(g19,g18)
    c: Coincident(g19,g17)
    c: Coincident(g19,g16)
    c: Coincident(g20,g21)
    c: Horizontal(g20)
    c: Vertical(g21)
    c: Coincident(g22,g21)
    c: Horizontal(g22)
    c: Coincident(g23,g20)
    c: Vertical(g23)
    c: Coincident(g23,g17)
    c: Coincident(g22,g16)
    c: PointOnObject(g24,g-4)
    c: Vertical(g24)
    c: PointOnObject(g25,g-5)
    c: Horizontal(g25)
    c: Radius(g26) = 3
    c: Tangent(g26,g24)
    c: Tangent(g26,g25)
    c: Coincident(g27,g26)
    c: PointOnObject(g27,g26)
    c: Coincident(g27,g24)
    c: Coincident(g27,g25)
    c: Coincident(g29,g28)
    c: Horizontal(g28)
    c: Vertical(g29)
    c: Coincident(g30,g29)
    c: Horizontal(g30)
    c: Coincident(g31,g28)
    c: Vertical(g31)
    c: Coincident(g31,g25)
    c: Coincident(g30,g24)
    c: Coincident(g0,g-3)
    c: Coincident(g1,g-6)
    c: Coincident(g-6,g16)
    c: Coincident(g17,g-5)
    c: Coincident(g-5,g25)
    c: Coincident(g-4,g24)
    c: Coincident(g9,g-4)
    c: Coincident(g8,g-3)
FEATURE [Sketcher::SketchObject] Sketch005
  ExternalGeometry = -> [Pocket001,Sketch]
  MapMode = 5
  Placement = pos=(0,0,8.5) rot=(0,0,1;0rad)
  Support = -> [Pocket001]
  sketch-geometry (10):
    g0: LineSegment [constr] StartX=-21.4583 StartY=31.2328 StartZ=0 EndX=-21.4583 EndY=-27.0552 EndZ=0
    g1: LineSegment [constr] StartX=-45.4064 StartY=-10.0606 StartZ=0 EndX=40.4454 EndY=-10.0606 EndZ=0
    g2: Circle [constr] CenterX=-21.4583 CenterY=-10.0606 CenterZ=0 NormalX=0 NormalY=0 NormalZ=1 AngleXU=0 Radius=6.2
    g3: LineSegment StartX=-12 StartY=8.5 StartZ=0 EndX=12 EndY=8.5 EndZ=0
    g4: LineSegment StartX=12 StartY=8.5 StartZ=0 EndX=12 EndY=-4.5 EndZ=0
    g5: LineSegment StartX=12 StartY=-4.5 StartZ=0 EndX=-12 EndY=-4.5 EndZ=0
    g6: LineSegment StartX=-12 StartY=-4.5 StartZ=0 EndX=-12 EndY=8.5 EndZ=0
    g7: LineSegment [constr] StartX=-29 StartY=24.9491 StartZ=0 EndX=-29 EndY=-20.674 EndZ=0
    g8: LineSegment [constr] StartX=-44.8443 StartY=11.5 StartZ=0 EndX=14.9752 EndY=11.5 EndZ=0
    g9: Circle CenterX=-21.4583 CenterY=-10.0606 CenterZ=0 NormalX=0 NormalY=0 NormalZ=1 AngleXU=0 Radius=6.2
  constraints (26):
    c: Coincident(g5,g6)
    c: Coincident(g3,g6)
    c: Coincident(g4,g5)
    c: Coincident(g3,g4)
    c: DistanceX(g3,g3) = 24
    c: DistanceY(g4,g4) = 13
    c: Vertical(g7)
    c: Horizontal(g8)
    c: PointOnObject(g-4,g8)
    c: PointOnObject(g-4,g7)
    c: PointOnObject(g2,g0)
    c: PointOnObject(g2,g1)
    c: DistanceX(g7,g0) = 7.54172
    c: DistanceX(g7,g3) = 17
    c: DistanceY(g3,g-4) = 3
    c: DistanceY(g1,g8) = 21.5606
    c: Vertical(g0)
    c: Horizontal(g1)
    c: Radius(g2) = 6.2
    c: Coincident(g9,g2)
    c: Radius(g9) = 6.2
    c: DistanceY(g-5,g-4) = 23
    c: Vertical(g4)
    c: Vertical(g6)
    c: Horizontal(g3)
    c: Horizontal(g5)
FEATURE [PartDesign::Pocket] Pocket002
  BaseFeature = -> Pocket001
  Length = 5
  Length2 = 100
  Profile = -> Sketch005
  Type = 0
FEATURE [Sketcher::SketchObject] Sketch006
  AttachmentOffset = pos=(7.7,0,0) rot=(0,0,1;0rad)
  ExternalGeometry = -> [Pocket002]
  MapMode = 5
  Placement = pos=(7.7,0,6.5) rot=(1,0,0;3.14159rad)
  Support = -> [Pocket002]
  sketch-geometry (4):
    g0: LineSegment StartX=-23.85 StartY=15.3 StartZ=0 EndX=8.15 EndY=15.3 EndZ=0
    g1: LineSegment StartX=8.15 StartY=15.3 StartZ=0 EndX=8.15 EndY=-15.3 EndZ=0
    g2: LineSegment StartX=8.15 StartY=-15.3 StartZ=0 EndX=-23.85 EndY=-15.3 EndZ=0
    g3: LineSegment StartX=-23.85 StartY=-15.3 StartZ=0 EndX=-23.85 EndY=15.3 EndZ=0
FEATURE [PartDesign::Pocket] Pocket003
  BaseFeature = -> Pocket002
  Length = 0.7
  Length2 = 100
  Profile = -> Sketch006
  Type = 0
FEATURE [PartDesign::Fillet] Fillet
  Base = -> Pocket003 [Edge38]
  BaseFeature = -> Pocket003
  Radius = 2
FEATURE [PartDesign::Chamfer] Chamfer
  Base = -> Fillet [Edge60,Edge61,Edge62,Edge63]
  BaseFeature = -> Fillet
  Size = 1
FEATURE [Sketcher::SketchObject] Sketch007
  MapMode = 5
  Placement = pos=(0,0,15.5) rot=(0,0,1;0rad)
  sketch-geometry (4):
    g0: Circle CenterX=34.8 CenterY=17.3 CenterZ=0 NormalX=0 NormalY=0 NormalZ=1 AngleXU=0 Radius=2.63102
    g1: Circle CenterX=-34.8 CenterY=17.3 CenterZ=0 NormalX=0 NormalY=0 NormalZ=1 AngleXU=0 Radius=2.66333
    g2: Circle CenterX=-34.8 CenterY=-17.3 CenterZ=0 NormalX=0 NormalY=0 NormalZ=1 AngleXU=0 Radius=2.82775
    g3: Circle CenterX=34.8 CenterY=-17.3 CenterZ=0 NormalX=0 NormalY=0 NormalZ=1 AngleXU=0 Radius=2.89107
FEATURE [PartDesign::Hole] Hole
  BaseFeature = -> Chamfer
  Depth = 20
  DepthType = 1
  Diameter = 3.3
  DrillPoint = 1
  DrillPointAngle = 118
  HoleCutCountersinkAngle = 90
  HoleCutDepth = 0
  HoleCutDiameter = 3
  HoleCutType = 0
  ModelActualThread = false
  Profile = -> Sketch007
  Tapered = false
  TaperedAngle = 90
  ThreadAngle = 60
  ThreadClass = 0
  ThreadCutOffInner = 0.0433013
  ThreadCutOffOuter = 0.0866025
  ThreadDirection = 0
  ThreadFit = 0
  ThreadPitch = 0.4
  ThreadSize = 3
  ThreadType = 1
  Threaded = false
FEATURE [Sketcher::SketchObject] Sketch008
  ExternalGeometry = -> [Hole]
  MapMode = 5
  Placement = pos=(0,0,8.5) rot=(0,0,1;0rad)
  Support = -> [Hole]
  sketch-geometry (4):
    g0: Circle CenterX=34.8 CenterY=17.3 CenterZ=0 NormalX=0 NormalY=0 NormalZ=1 AngleXU=0 Radius=2.8
    g1: Circle CenterX=34.8 CenterY=-17.3 CenterZ=0 NormalX=0 NormalY=0 NormalZ=1 AngleXU=0 Radius=2.8
    g2: Circle CenterX=-34.8 CenterY=-17.3 CenterZ=0 NormalX=0 NormalY=0 NormalZ=1 AngleXU=0 Radius=2.8
    g3: Circle CenterX=-34.8 CenterY=17.3 CenterZ=0 NormalX=0 NormalY=0 NormalZ=1 AngleXU=0 Radius=2.8
  constraints (7):
    c: Coincident(g0,g-5)
    c: Coincident(g1,g-8)
    c: Coincident(g3,g-6)
    c: Radius(g3) = 2.8
    c: Radius(g0) = 2.8
    c: Radius(g2) = 2.8
    c: Radius(g1) = 2.8
FEATURE [PartDesign::Pocket] Pocket004
  BaseFeature = -> Hole
  Length = 3.3
  Length2 = 100
  Profile = -> Sketch008
  Type = 0
FEATURE [Sketcher::SketchObject] Sketch009
  MapMode = 5
  Placement = pos=(0,0,8.5) rot=(0,0,1;0rad)
  expr: Constraints[7] = Sketch.Constraints[9]
  expr: Constraints[40] = Sketch.Constraints[42]
  expr: Constraints[18] = Sketch.Constraints[20]
  expr: Constraints[19] = Sketch.Constraints[21]
  expr: Constraints[29] = Sketch.Constraints[31]
  expr: Constraints[27] = Sketch.Constraints[29]
  expr: Constraints[28] = Sketch.Constraints[30]
  expr: Constraints[26] = Sketch.Constraints[28]
  expr: Constraints[6] = Sketch.Constraints[8]
  expr: Constraints[38] = Sketch.Constraints[40]
  expr: Constraints[47] = Sketch.Constraints[49]
  expr: Constraints[39] = Sketch.Constraints[41]
  expr: Constraints[49] = Sketch.Constraints[51]
  expr: Constraints[45] = Sketch.Constraints[47]
  expr: Constraints[43] = Sketch.Constraints[45]
  expr: Constraints[41] = Sketch.Constraints[43]
  sketch-geometry (62):
    g0: LineSegment [constr] StartX=-32.5 StartY=15 StartZ=0 EndX=32.5 EndY=15 EndZ=0
    g1: LineSegment [constr] StartX=32.5 StartY=15 StartZ=0 EndX=32.5 EndY=-15 EndZ=0
    g2: LineSegment [constr] StartX=32.5 StartY=-15 StartZ=0 EndX=-32.5 EndY=-15 EndZ=0
    g3: LineSegment [constr] StartX=-32.5 StartY=-15 StartZ=0 EndX=-32.5 EndY=15 EndZ=0
    g4: LineSegment [constr] StartX=-29 StartY=11.5 StartZ=0 EndX=29 EndY=11.5 EndZ=0
    g5: LineSegment [constr] StartX=29 StartY=11.5 StartZ=0 EndX=29 EndY=-11.5 EndZ=0
    g6: LineSegment [constr] StartX=29 StartY=-11.5 StartZ=0 EndX=-29 EndY=-11.5 EndZ=0
    g7: LineSegment [constr] StartX=-29 StartY=-11.5 StartZ=0 EndX=-29 EndY=11.5 EndZ=0
    g8: Circle [constr] CenterX=-29 CenterY=11.5 CenterZ=0 NormalX=0 NormalY=0 NormalZ=1 AngleXU=0 Radius=1.375
    g9: Circle [constr] CenterX=29 CenterY=11.5 CenterZ=0 NormalX=0 NormalY=0 NormalZ=1 AngleXU=0 Radius=1.375
    g10: Circle [constr] CenterX=29 CenterY=-11.5 CenterZ=0 NormalX=0 NormalY=0 NormalZ=1 AngleXU=0 Radius=1.375
    g11: Circle [constr] CenterX=-29 CenterY=-11.5 CenterZ=0 NormalX=0 NormalY=0 NormalZ=1 AngleXU=0 Radius=1.375
    g12: LineSegment [constr] StartX=-29.5 StartY=12 StartZ=0 EndX=29.5 EndY=12 EndZ=0
    g13: LineSegment [constr] StartX=29.5 StartY=12 StartZ=0 EndX=29.5 EndY=-12 EndZ=0
    g14: LineSegment [constr] StartX=29.5 StartY=-12 StartZ=0 EndX=-29.5 EndY=-12 EndZ=0
    g15: LineSegment [constr] StartX=-29.5 StartY=-12 StartZ=0 EndX=-29.5 EndY=12 EndZ=0
    g16: ArcOfCircle [constr] CenterX=-29.5 CenterY=12 CenterZ=0 NormalX=0 NormalY=0 NormalZ=1 AngleXU=0 Radius=3 StartAngle=1.5708 EndAngle=3.14159
    g17: ArcOfCircle [constr] CenterX=29.5 CenterY=12 CenterZ=0 NormalX=0 NormalY=0 NormalZ=1 AngleXU=0 Radius=3 StartAngle=5.0002e-08 EndAngle=1.5708
    g18: ArcOfCircle [constr] CenterX=29.5 CenterY=-12 CenterZ=0 NormalX=0 NormalY=0 NormalZ=1 AngleXU=0 Radius=3 StartAngle=4.71239 EndAngle=6.28319
    g19: ArcOfCircle [constr] CenterX=-29.5 CenterY=-12 CenterZ=0 NormalX=0 NormalY=0 NormalZ=1 AngleXU=0 Radius=3 StartAngle=3.14159 EndAngle=4.71239
    g20: LineSegment [constr] StartX=-29.5 StartY=15 StartZ=0 EndX=29.5 EndY=15 EndZ=0
    g21: LineSegment [constr] StartX=32.5 StartY=12 StartZ=0 EndX=32.5 EndY=-12 EndZ=0
    g22: LineSegment [constr] StartX=29.5 StartY=-15 StartZ=0 EndX=-29.5 EndY=-15 EndZ=0
    g23: LineSegment [constr] StartX=-32.5 StartY=-12 StartZ=0 EndX=-32.5 EndY=12 EndZ=0
    g24: LineSegment [constr] StartX=25.3417 StartY=8.13712 StartZ=0 EndX=27.8417 EndY=8.13712 EndZ=0
    g25: LineSegment [constr] StartX=27.8417 StartY=8.13712 StartZ=0 EndX=27.8417 EndY=-1.46288 EndZ=0
    g26: LineSegment [constr] StartX=27.8417 StartY=-1.46288 StartZ=0 EndX=25.3417 EndY=-1.46288 EndZ=0
    g27: LineSegment [constr] StartX=25.3417 StartY=-1.46288 StartZ=0 EndX=25.3417 EndY=8.13712 EndZ=0
    g28: LineSegment [constr] StartX=25.3417 StartY=6.93712 StartZ=0 EndX=27.8417 EndY=6.93712 EndZ=0
    g29: LineSegment [constr] StartX=25.3417 StartY=5.73712 StartZ=0 EndX=27.8417 EndY=5.73712 EndZ=0
    g30: LineSegment [constr] StartX=25.3417 StartY=4.53712 StartZ=0 EndX=27.8417 EndY=4.53712 EndZ=0
    g31: LineSegment [constr] StartX=25.3417 StartY=3.33712 StartZ=0 EndX=27.8417 EndY=3.33712 EndZ=0
    g32: LineSegment [constr] StartX=25.3417 StartY=2.13712 StartZ=0 EndX=27.8417 EndY=2.13712 EndZ=0
    g33: LineSegment [constr] StartX=25.3417 StartY=0.937121 StartZ=0 EndX=27.8417 EndY=0.937121 EndZ=0
    g34: LineSegment [constr] StartX=25.3417 StartY=-0.262879 StartZ=0 EndX=27.8417 EndY=-0.262879 EndZ=0
    g35: ArcOfCircle CenterX=25.3417 CenterY=8.13712 CenterZ=0 NormalX=0 NormalY=0 NormalZ=1 AngleXU=0 Radius=0.75 StartAngle=1.12328 EndAngle=4.26487
    g36: ArcOfCircle CenterX=27.8417 CenterY=6.93712 CenterZ=0 NormalX=0 NormalY=0 NormalZ=1 AngleXU=0 Radius=0.75 StartAngle=4.26487 EndAngle=7.40646
    g37: Circle [constr] CenterX=27.8417 CenterY=6.93712 CenterZ=0 NormalX=0 NormalY=0 NormalZ=1 AngleXU=0 Radius=0.75
    g38: Circle [constr] CenterX=25.3417 CenterY=8.13712 CenterZ=0 NormalX=0 NormalY=0 NormalZ=1 AngleXU=0 Radius=0.75
    g39: LineSegment [constr] StartX=25.4338 StartY=8.92483 StartZ=0 EndX=28.7439 EndY=7.33601 EndZ=0
    g40: LineSegment [constr] StartX=24.2457 StartY=7.83129 StartZ=0 EndX=27.5618 EndY=6.23954 EndZ=0
    g41: LineSegment StartX=25.6663 StartY=8.81326 StartZ=0 EndX=28.1663 EndY=7.61326 EndZ=0
    g42: LineSegment StartX=25.0172 StartY=7.46098 StartZ=0 EndX=27.5172 EndY=6.26098 EndZ=0
    g43: ArcOfCircle CenterX=25.3417 CenterY=5.73712 CenterZ=0 NormalX=0 NormalY=0 NormalZ=1 AngleXU=0 Radius=0.75 StartAngle=1.12852 EndAngle=4.25962
    g44: LineSegment StartX=25.6627 StartY=6.41496 StartZ=0 EndX=28.149 EndY=5.22128 EndZ=0
    g45: ArcOfCircle CenterX=27.8417 CenterY=4.53712 CenterZ=0 NormalX=0 NormalY=0 NormalZ=1 AngleXU=0 Radius=0.75 StartAngle=4.23957 EndAngle=7.43184
    g46: LineSegment StartX=25.0136 StartY=5.06269 StartZ=0 EndX=27.5002 EndY=3.86941 EndZ=0
    g47: Circle CenterX=25.3417 CenterY=-1.46288 CenterZ=0 NormalX=0 NormalY=0 NormalZ=1 AngleXU=0 Radius=0.75
    g48: Circle CenterX=27.8417 CenterY=-0.262879 CenterZ=0 NormalX=0 NormalY=0 NormalZ=1 AngleXU=0 Radius=0.75
    g49: Circle CenterX=25.3417 CenterY=0.937121 CenterZ=0 NormalX=0 NormalY=0 NormalZ=1 AngleXU=0 Radius=0.75
    g50: Circle CenterX=27.8417 CenterY=2.13712 CenterZ=0 NormalX=0 NormalY=0 NormalZ=1 AngleXU=0 Radius=0.75
    g51: Circle CenterX=25.3417 CenterY=3.33712 CenterZ=0 NormalX=0 NormalY=0 NormalZ=1 AngleXU=0 Radius=0.75
    g52: LineSegment [constr] StartX=25.8911 StartY=-2.0311 StartZ=0 EndX=28.1814 EndY=-0.931754 EndZ=0
    g53: LineSegment [constr] StartX=24.1632 StartY=-1.19664 StartZ=0 EndX=27.4908 EndY=0.400624 EndZ=0
    g54: LineSegment [constr] StartX=24.363 StartY=0.574977 StartZ=0 EndX=28.2413 EndY=-1.28662 EndZ=0
    g55: LineSegment [constr] StartX=25.6678 StartY=1.61253 StartZ=0 EndX=28.5751 EndY=0.217016 EndZ=0
    g56: LineSegment [constr] StartX=24.9997 StartY=-0.0589725 StartZ=0 EndX=28.6995 EndY=1.71693 EndZ=0
    g57: LineSegment [constr] StartX=24.1511 StartY=1.19754 StartZ=0 EndX=27.2971 EndY=2.70762 EndZ=0
    g58: LineSegment [constr] StartX=24.3738 StartY=2.96979 StartZ=0 EndX=27.5399 EndY=1.45005 EndZ=0
    g59: Circle [constr] CenterX=25.3417 CenterY=2.13712 CenterZ=0 NormalX=0 NormalY=0 NormalZ=1 AngleXU=0 Radius=0.331828
    g60: Circle [constr] CenterX=27.8417 CenterY=0.937121 CenterZ=0 NormalX=0 NormalY=0 NormalZ=1 AngleXU=0 Radius=0.331828
    g61: Circle [constr] CenterX=25.3417 CenterY=-0.262879 CenterZ=0 NormalX=0 NormalY=0 NormalZ=1 AngleXU=0 Radius=0.331828
  constraints (163):
    c: Coincident(g0,g1)
    c: Coincident(g1,g2)
    c: Coincident(g2,g3)
    c: Coincident(g3,g0)
    c: Horizontal(g2)
    c: Vertical(g3)
    c: DistanceX(g0,g0) = 65
    c: DistanceY(g1,g1) = 30
    c: Symmetric(g0,g0,g-2)
    c: Symmetric(g0,g1,g-1)
    c: Coincident(g4,g5)
    c: Coincident(g5,g6)
    c: Coincident(g6,g7)
    c: Coincident(g7,g4)
    c: Horizontal(g4)
    c: Horizontal(g6)
    c: Vertical(g5)
    c: Vertical(g7)
    c: DistanceX(g4,g4) = 58
    c: DistanceY(g5,g5) = 23
    c: Symmetric(g4,g5,g-1)
    c: Symmetric(g4,g4,g-2)
    c: Coincident(g8,g4)
    c: Coincident(g9,g4)
    c: Coincident(g10,g5)
    c: Coincident(g11,g6)
    c: Radius(g11) = 1.375
    c: Radius(g8) = 1.375
    c: Radius(g9) = 1.375
    c: Radius(g10) = 1.375
    c: Coincident(g12,g13)
    c: Coincident(g13,g14)
    c: Coincident(g14,g15)
    c: Coincident(g15,g12)
    c: Horizontal(g12)
    c: Horizontal(g14)
    c: Vertical(g13)
    c: Vertical(g15)
    c: DistanceX(g4,g12) = 0.5
    c: DistanceY(g4,g12) = 0.5
    c: DistanceY(g13,g5) = 0.5
    c: DistanceX(g14,g6) = 0.5
    c: Coincident(g16,g12)
    c: Radius(g16) = 3
    c: Coincident(g17,g12)
    c: Radius(g17) = 3
    c: Coincident(g18,g13)
    c: Radius(g18) = 3
    c: Coincident(g19,g14)
    c: Radius(g19) = 3
    c: PointOnObject(g16,g0)
    c: PointOnObject(g17,g1)
    c: PointOnObject(g18,g2)
    c: PointOnObject(g19,g3)
    c: Coincident(g20,g16)
    c: Horizontal(g20)
    c: Coincident(g20,g17)
    c: Coincident(g21,g17)
    c: Vertical(g21)
    c: Coincident(g18,g21)
    c: Coincident(g22,g18)
    c: Horizontal(g22)
    c: Coincident(g19,g22)
    c: Coincident(g23,g19)
    c: Vertical(g23)
    c: Coincident(g23,g16)
    c: Coincident(g24,g25)
    c: Coincident(g25,g26)
    c: Coincident(g26,g27)
    c: Coincident(g27,g24)
    c: Horizontal(g24)
    c: Horizontal(g26)
    c: Vertical(g25)
    c: Vertical(g27)
    c: DistanceX(g4,g24) = 54.3417  '3,362879'
    c: DistanceX(g24,g24) = 2.5
    c: DistanceY(g27,g27) = 9.6
    c: DistanceY(g24,g4) = 3.36288
    c: Horizontal(g28)
    c: Horizontal(g29)
    c: Horizontal(g30)
    c: Horizontal(g32)
    c: Horizontal(g33)
    c: DistanceY(g28,g24) = 1.2
    c: DistanceY(g29,g28) = 1.2
    c: DistanceY(g30,g29) = 1.2
    c: DistanceY(g31,g30) = 1.2
    c: DistanceY(g32,g31) = 1.2
    c: DistanceY(g33,g32) = 1.2
    c: Horizontal(g34)
    c: DistanceY(g34,g33) = 1.2
    c: PointOnObject(g28,g27)
    c: PointOnObject(g29,g27)
    c: PointOnObject(g30,g27)
    c: PointOnObject(g31,g27)
    c: PointOnObject(g32,g27)
    c: PointOnObject(g33,g27)
    c: PointOnObject(g34,g27)
    c: PointOnObject(g34,g25)
    c: PointOnObject(g33,g25)
    c: PointOnObject(g32,g25)
    c: PointOnObject(g31,g25)
    c: PointOnObject(g30,g25)
    c: PointOnObject(g29,g25)
    c: PointOnObject(g28,g25)
    c: Coincident(g35,g24)
    c: Coincident(g36,g28)
    c: Radius(g35) = 0.75
    c: Radius(g36) = 0.75
    c: Coincident(g37,g28)
    c: Coincident(g38,g24)
    c: Radius(g38) = 0.75
    c: Radius(g37) = 0.75
    c: Tangent(g39,g37)
    c: Tangent(g39,g38)
    c: Tangent(g40,g38)
    c: Tangent(g40,g37)
    c: PointOnObject(g41,g39)
    c: PointOnObject(g41,g39)
    c: PointOnObject(g42,g40)
    c: PointOnObject(g42,g40)
    c: Coincident(g41,g35)
    c: Coincident(g35,g42)
    c: Coincident(g41,g36)
    c: Coincident(g36,g42)
    c: Equal(g35,g43) = 0.75
    c: Equal(g36,g45) = 0.75
    c: Coincident(g44,g43)
    c: Coincident(g43,g46)
    c: Coincident(g44,g45)
    c: Coincident(g45,g46)
    c: Coincident(g43,g29)
    c: Coincident(g45,g30)
    c: Coincident(g48,g34)
    c: Coincident(g49,g33)
    c: Coincident(g50,g32)
    c: Coincident(g51,g31)
    c: Radius(g51) = 0.75
    c: Radius(g50) = 0.75
    c: Radius(g49) = 0.75
    c: Radius(g48) = 0.75
    c: Radius(g47) = 0.75
    c: Tangent(g55,g48)
    c: Tangent(g55,g49)
    c: Tangent(g54,g49)
    c: Tangent(g54,g48)
    c: Tangent(g53,g47)
    c: Tangent(g53,g48)
    c: Coincident(g47,g26)
    c: Tangent(g47,g52)
    c: Tangent(g52,g48)
    c: Tangent(g56,g49)
    c: Tangent(g56,g50)
    c: Tangent(g57,g50)
    c: Tangent(g57,g49)
    c: Tangent(g58,g51)
    c: Tangent(g58,g50)
    c: Coincident(g59,g32)
    c: Tangent(g59,g58)
    c: Coincident(g60,g33)
    c: Tangent(g60,g56)
    c: Coincident(g61,g34)
    c: Tangent(g61,g54)
FEATURE [PartDesign::Pocket] Pocket005
  BaseFeature = -> Pocket004
  Length = 5
  Length2 = 100
  Profile = -> Sketch009
  Type = 2
FEATURE [Part::Feature] path76
  shape: bbox 67.53 x 33.36 x 2e-07 mm, 1 faces, 0 solids (baked)
FEATURE [Part::Feature] path76001
  shape: bbox 56.51 x 33.36 x 2e-07 mm, 1 faces, 0 solids (baked)
FEATURE [Part::Feature] path76002
  shape: bbox 67.23 x 33.39 x 2e-07 mm, 1 faces, 0 solids (baked)
FEATURE [Part::Feature] path76003
  shape: bbox 86.8 x 33.05 x 2e-07 mm, 1 faces, 0 solids (baked)
FEATURE [Part::Feature] path76004
  shape: bbox 24.36 x 17.06 x 2e-07 mm, 1 faces, 0 solids (baked)
FEATURE [Part::Cut] Cut
  Base = -> path76003
  Tool = -> path76004
FEATURE [Part::MultiFuse] Fusion
  Shapes = -> [path76,path76001,path76002,Cut]
FEATURE [Part::FeaturePython] Scale001  # Draft clone (typed FeaturePython)
  Fuse = false
  Objects = -> [Fusion]
  Placement = pos=(-20,0,14.85) rot=(0,0,1;0rad)
  Scale = (0.18,0.18,0.18)
FEATURE [Sketcher::SketchObject] Sketch010
  MapMode = 5
  Placement = pos=(0,0,8.5) rot=(0,0,1;0rad)
FEATURE [Part::FeaturePython] Scale  # Draft clone (typed FeaturePython)
  Fuse = false
  Objects = -> [Scale001]
  Placement = pos=(-11.9,-2.3,7.95) rot=(0,0,1;0rad)
  Scale = (0.8,0.8,0.8)
FEATURE [PartDesign::Fillet] Fillet001
  Base = -> Pocket005 [Edge33,Edge34,Edge21,Edge20,Edge22,Edge23,Edge27,Edge102,Edge94,Edge92,Edge88,Edge116,Edge90,Edge114]
  BaseFeature = -> Pocket005
  Radius = 0.2
FEATURE [PartDesign::Fillet] Fillet003
  Base = -> Fillet001 [Edge22,Edge21,Edge28,Edge27]
  BaseFeature = -> Fillet001
  Radius = 0.1
FEATURE [PartDesign::Fillet] Fillet004
  Base = -> Fillet003 [Edge241,Edge246,Edge247,Edge245,Edge236]
  BaseFeature = -> Fillet003
  Radius = 0.1
FEATURE [PartDesign::Body] Body
  Group = -> [Sketch,Sketch001,Pad,Sketch002,Pocket,Sketch003,Pocket001,Sketch004,Sketch005,Pocket002,Sketch006,Pocket003,Fillet,Chamfer,Sketch007,Hole,Sketch008,Pocket004,Sketch009,Pocket005,Sketch010,Fillet001,Fillet003,Fillet004]
  Origin = -> Origin
  Tip = -> Fillet004
FEATURE [Part::Extrusion] Extrude
  Base = -> Scale
  Dir = (0,0,1)
  DirMode = 0
  FaceMakerClass = Part::FaceMakerBullseye
  LengthFwd = 5
  LengthRev = 0
  Solid = false
  Symmetric = false
FEATURE [Part::Cut] Cut001
  Base = -> Fillet004
  Tool = -> Extrude
FEATURE [Mesh::Feature] Mesh  label="Cut001 (Meshed)"
